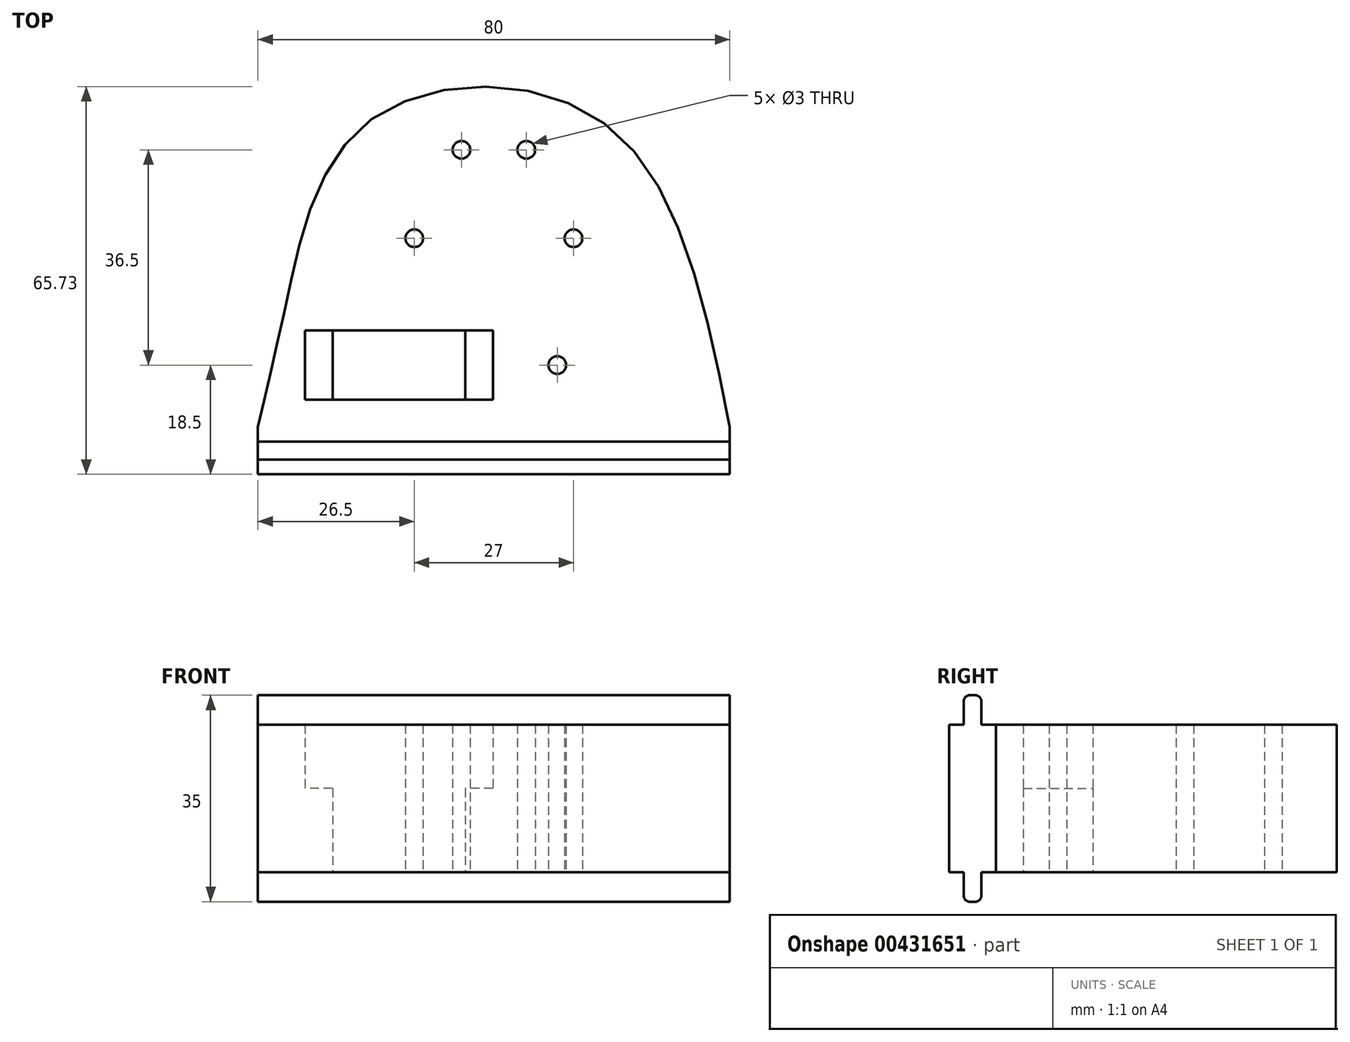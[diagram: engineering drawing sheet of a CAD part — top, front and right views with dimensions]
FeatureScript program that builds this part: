
annotation { "Feature Type Name" : "Feature", "Feature Type Description" : "" }
export const myFeature = defineFeature(function(context is Context, id is Id, definition is map)
    precondition{}
    {
        {
            var Q0;
            Q0=qCreatedBy(makeId("Top.planeOp"),FACE);
            var sketch = newSketch(context, id + "F0", { "sketchPlane" : qUnion([Q0])});
            skLineSegment(sketch, "E0.bottom", {"start": v(0, 0) * mm, "end": v(80, 0) * mm});
            skLineSegment(sketch, "E0.top", {"start": v(0, 40) * mm, "end": v(80, 40) * mm});
            skLineSegment(sketch, "E0.left", {"start": v(0, 0) * mm, "end": v(0, 40) * mm});
            skLineSegment(sketch, "E0.right", {"start": v(80, 0) * mm, "end": v(80, 40) * mm});
            skLineSegment(sketch, "E1", {"start": v(40, 0) * mm, "end": v(40, 10) * mm});
            skLineSegment(sketch, "E2", {"start": v(40, 10) * mm, "end": v(26.5, 10) * mm});
            skLineSegment(sketch, "E3", {"start": v(26.5, 10) * mm, "end": v(53.5, 10) * mm});
            skCircle(sketch, "E4", {"center": v(26.5, 10) * mm, "radius": 1.5 * mm});
            skCircle(sketch, "E5", {"center": v(53.5, 10) * mm, "radius": 1.5 * mm});
            skLineSegment(sketch, "E6.bottom", {"start": v(26.5, 10) * mm, "end": v(34.5, 10) * mm});
            skLineSegment(sketch, "E6.top", {"start": v(26.5, 25) * mm, "end": v(34.5, 25) * mm, "construction": true});
            skLineSegment(sketch, "E6.left", {"start": v(26.5, 10) * mm, "end": v(26.5, 25) * mm, "construction": true});
            skLineSegment(sketch, "E6.right", {"start": v(34.5, 10) * mm, "end": v(34.5, 25) * mm});
            skLineSegment(sketch, "E7.bottom", {"start": v(53.5, 10) * mm, "end": v(45.5, 10) * mm});
            skLineSegment(sketch, "E7.top", {"start": v(53.5, 25) * mm, "end": v(45.5, 25) * mm});
            skLineSegment(sketch, "E7.left", {"start": v(53.5, 10) * mm, "end": v(53.5, 25) * mm, "construction": true});
            skLineSegment(sketch, "E7.right", {"start": v(45.5, 10) * mm, "end": v(45.5, 25) * mm});
            skCircle(sketch, "E8", {"center": v(34.5, 25) * mm, "radius": 1.5 * mm});
            skCircle(sketch, "E9", {"center": v(45.5, 25) * mm, "radius": 1.5 * mm});
            skLineSegment(sketch, "E10.top", {"start": v(0, -30) * mm, "end": v(80, -30) * mm});
            skLineSegment(sketch, "E10.left", {"start": v(0, 0) * mm, "end": v(0, -30) * mm});
            skLineSegment(sketch, "E10.right", {"start": v(80, 0) * mm, "end": v(80, -30) * mm});
            skLineSegment(sketch, "E11.bottom", {"start": v(26.5, 10) * mm, "end": v(29.25, 10) * mm, "construction": true});
            skLineSegment(sketch, "E11.top", {"start": v(26.5, -11.5) * mm, "end": v(29.25, -11.5) * mm, "construction": true});
            skLineSegment(sketch, "E11.left", {"start": v(26.5, 10) * mm, "end": v(26.5, -11.5) * mm, "construction": true});
            skLineSegment(sketch, "E11.right", {"start": v(29.25, 10) * mm, "end": v(29.25, -11.5) * mm, "construction": true});
            skLineSegment(sketch, "E12.bottom", {"start": v(53.5, 10) * mm, "end": v(50.75, 10) * mm, "construction": true});
            skLineSegment(sketch, "E12.top", {"start": v(53.5, -11.5) * mm, "end": v(50.75, -11.5) * mm, "construction": true});
            skLineSegment(sketch, "E12.left", {"start": v(53.5, 10) * mm, "end": v(53.5, -11.5) * mm, "construction": true});
            skLineSegment(sketch, "E12.right", {"start": v(50.75, 10) * mm, "end": v(50.75, -11.5) * mm, "construction": true});
            skCircle(sketch, "E13", {"center": v(29.25, -11.5) * mm, "radius": 1.5 * mm});
            skCircle(sketch, "E14", {"center": v(50.75, -11.5) * mm, "radius": 1.5 * mm});
            skLineSegment(sketch, "E15", {"start": v(29.25, -11.5) * mm, "end": v(39.85, -11.5) * mm});
            skLineSegment(sketch, "E16", {"start": v(39.85, -11.5) * mm, "end": v(39.85, -17.4) * mm});
            skLineSegment(sketch, "E17.bottom", {"start": v(39.85, -17.4) * mm, "end": v(7.95, -17.4) * mm});
            skLineSegment(sketch, "E17.top", {"start": v(39.85, -5.6) * mm, "end": v(7.95, -5.6) * mm});
            skLineSegment(sketch, "E17.left", {"start": v(39.85, -17.4) * mm, "end": v(39.85, -5.6) * mm});
            skLineSegment(sketch, "E17.right", {"start": v(7.95, -17.4) * mm, "end": v(7.95, -5.6) * mm});
            skLineSegment(sketch, "E18", {"start": v(29.25, -11.5) * mm, "end": v(35.15, -11.5) * mm});
            skLineSegment(sketch, "E19", {"start": v(35.15, -11.5) * mm, "end": v(35.15, -17.4) * mm});
            skLineSegment(sketch, "E20.bottom", {"start": v(35.15, -17.4) * mm, "end": v(12.65, -17.4) * mm});
            skLineSegment(sketch, "E20.top", {"start": v(35.15, -5.6) * mm, "end": v(12.65, -5.6) * mm});
            skLineSegment(sketch, "E20.left", {"start": v(35.15, -17.4) * mm, "end": v(35.15, -5.6) * mm});
            skLineSegment(sketch, "E20.right", {"start": v(12.65, -17.4) * mm, "end": v(12.65, -5.6) * mm});
            skSolve(sketch);
        }
        {
            var Q0;
            Q0=makeQuery(id+"F0.imprint","IMPRINT",FACE,{"disambiguationData":[TD([[makeQuery(id+"F0.imprint","IMPRINT",EDGE,{"derivedFrom":sQuery(id+"F0.wireOp",EDGE,"E0.top")}),-1.0]])]});
            extrude(context, id + "F1", {"entities" : qUnion([Q0]), "depth" : 25 * mm});
        }
        {
            var Q0;
            Q0=makeQuery(id+"F0.imprint","IMPRINT",FACE,{"disambiguationData":[TD([[makeQuery(id+"F0.imprint","IMPRINT",EDGE,{"derivedFrom":sQuery(id+"F0.wireOp",EDGE,"E10.top")}),1.0]])]});
            extrude(context, id + "F2", {"entities" : qUnion([Q0]), "operationType" : NewBodyOperationType.ADD, "depth" : 25 * mm});
        }
        {
            var Q0;
            {var subQ0=sQuery(id+"F0.wireOp",EDGE,"E17.right");Q0=makeQuery(id+"F0.imprint","IMPRINT",FACE,{"disambiguationData":[TD([[makeQuery(id+"F0.imprint","IMPRINT",EDGE,{"derivedFrom":subQ0}),-1.0]])]});}
            var Q1;
            {var subQ0=sQuery(id+"F0.wireOp",EDGE,"E15");Q1=makeQuery(id+"F0.imprint","IMPRINT",FACE,{"disambiguationData":[TD([[makeQuery(id+"F0.imprint","IMPRINT",EDGE,{"derivedFrom":subQ0}),1.0]])]});}
            var Q2;
            {var subQ0=sQuery(id+"F0.wireOp",EDGE,"E15");Q2=makeQuery(id+"F0.imprint","IMPRINT",FACE,{"disambiguationData":[TD([[makeQuery(id+"F0.imprint","IMPRINT",EDGE,{"derivedFrom":subQ0}),-1.0]])]});}
            extrude(context, id + "F3", {"entities" : qUnion([Q0, Q1, Q2]), "operationType" : NewBodyOperationType.ADD, "depth" : 14.2 * mm});
        }
        {
            var Q0;
            {var subQ0=sQuery(id+"F0.wireOp",EDGE,"E0.bottom");Q0=makeQuery(id+"F2.boolean.opBoolean","MERGE",FACE,{"derivedFrom":[makeQuery(id+"F1.opExtrude","CAP_FACE",FACE,{"disambiguationData":[OSD([sQuery(id+"F0.wireOp",EDGE,"E0.top"),sQuery(id+"F0.wireOp",EDGE,"E0.left"),sQuery(id+"F0.wireOp",EDGE,"E0.right"),sQuery(id+"F0.wireOp",EDGE,"E4"),sQuery(id+"F0.wireOp",EDGE,"E5"),sQuery(id+"F0.wireOp",EDGE,"E8"),sQuery(id+"F0.wireOp",EDGE,"E9"),subQ0])],"isStart":false}),makeQuery(id+"F2.opExtrude","CAP_FACE",FACE,{"disambiguationData":[OSD([subQ0,sQuery(id+"F0.wireOp",EDGE,"E10.top"),sQuery(id+"F0.wireOp",EDGE,"E10.left"),sQuery(id+"F0.wireOp",EDGE,"E10.right"),sQuery(id+"F0.wireOp",EDGE,"E14"),sQuery(id+"F0.wireOp",EDGE,"E17.bottom"),sQuery(id+"F0.wireOp",EDGE,"E17.top"),sQuery(id+"F0.wireOp",EDGE,"E17.left"),sQuery(id+"F0.wireOp",EDGE,"E17.right"),sQuery(id+"F0.wireOp",EDGE,"E20.bottom"),sQuery(id+"F0.wireOp",EDGE,"E20.top")])],"isStart":false})]});}
            var sketch = newSketch(context, id + "F4", { "sketchPlane" : qUnion([Q0])});
            skLineSegment(sketch, "E21.bottom", {"start": v(0, -30) * mm, "end": v(4, -30) * mm, "construction": true});
            skLineSegment(sketch, "E21.top", {"start": v(0, -22) * mm, "end": v(4, -22) * mm, "construction": true});
            skLineSegment(sketch, "E21.left", {"start": v(0, -30) * mm, "end": v(0, -22) * mm, "construction": true});
            skLineSegment(sketch, "E21.right", {"start": v(4, -30) * mm, "end": v(4, -22) * mm, "construction": true});
            skLineSegment(sketch, "E22.bottom", {"start": v(80, -30) * mm, "end": v(61, -30) * mm, "construction": true});
            skLineSegment(sketch, "E22.top", {"start": v(80, -15) * mm, "end": v(61, -15) * mm, "construction": true});
            skLineSegment(sketch, "E22.left", {"start": v(80, -30) * mm, "end": v(80, -15) * mm, "construction": true});
            skLineSegment(sketch, "E22.right", {"start": v(61, -30) * mm, "end": v(61, -15) * mm, "construction": true});
            skLineSegment(sketch, "E23.bottom", {"start": v(80, 40) * mm, "end": v(58, 40) * mm, "construction": true});
            skLineSegment(sketch, "E23.top", {"start": v(80, 30) * mm, "end": v(58, 30) * mm, "construction": true});
            skLineSegment(sketch, "E23.left", {"start": v(80, 40) * mm, "end": v(80, 30) * mm, "construction": true});
            skLineSegment(sketch, "E23.right", {"start": v(58, 40) * mm, "end": v(58, 30) * mm, "construction": true});
            skLineSegment(sketch, "E24.bottom", {"start": v(0, 40) * mm, "end": v(19, 40) * mm, "construction": true});
            skLineSegment(sketch, "E24.top", {"start": v(0, 30) * mm, "end": v(19, 30) * mm, "construction": true});
            skLineSegment(sketch, "E24.left", {"start": v(0, 40) * mm, "end": v(0, 30) * mm, "construction": true});
            skLineSegment(sketch, "E24.right", {"start": v(19, 40) * mm, "end": v(19, 30) * mm, "construction": true});
            skLineSegment(sketch, "E25", {"start": v(0, 0) * mm, "end": v(5, 0) * mm, "construction": true});
            skLineSegment(sketch, "E26", {"start": v(80, -30) * mm, "end": v(80, -22) * mm});
            skFitSpline(sketch, "E27", {"points": [v(0, -22) * mm, v(5, 0) * mm, v(19, 30) * mm, v(58, 30) * mm, v(80, -22) * mm], "startDerivative": vector(24.26, 103.47) * mm, "endDerivative": vector(40.81, -206.26) * mm});
            skLineSegment(sketch, "E28", {"start": v(0, -30) * mm, "end": v(0, -27.5) * mm});
            skLineSegment(sketch, "E29.bottom", {"start": v(0, -27.5) * mm, "end": v(80, -27.5) * mm});
            skLineSegment(sketch, "E29.top", {"start": v(0, -24.5) * mm, "end": v(80, -24.5) * mm});
            skLineSegment(sketch, "E29.left", {"start": v(0, -27.5) * mm, "end": v(0, -24.5) * mm});
            skLineSegment(sketch, "E29.right", {"start": v(80, -27.5) * mm, "end": v(80, -24.5) * mm});
            skSolve(sketch);
        }
        {
            var Q0;
            {var subQ0=sQuery(id+"F4.wireOp",EDGE,"E27");Q0=makeQuery(id+"F4.imprint","IMPRINT",FACE,{"disambiguationData":[TD([[makeQuery(id+"F4.imprint","IMPRINT",EDGE,{"derivedFrom":subQ0}),1.0]])]});}
            extrude(context, id + "F5", {"entities" : qUnion([Q0]), "operationType" : NewBodyOperationType.REMOVE, "oppositeDirection" : true, "depth" : 25 * mm});
        }
        {
            var Q0;
            Q0=makeQuery(id+"F4.imprint","IMPRINT",FACE,{"disambiguationData":[TD([[makeQuery(id+"F4.imprint","IMPRINT",EDGE,{"derivedFrom":sQuery(id+"F4.wireOp",EDGE,"E29.bottom")}),1.0]])]});
            extrude(context, id + "F6", {"entities" : qUnion([Q0]), "operationType" : NewBodyOperationType.ADD, "depth" : 5 * mm});
        }
        {
            var Q0;
            Q0=makeQuery(id+"F6.opExtrude","CAP_FACE",FACE,{"disambiguationData":[OSD([sQuery(id+"F4.wireOp",EDGE,"E29.bottom"),sQuery(id+"F4.wireOp",EDGE,"E29.top"),sQuery(id+"F4.wireOp",EDGE,"E29.left"),sQuery(id+"F4.wireOp",EDGE,"E29.right")])],"isStart":false});
            extrude(context, id + "F7", {"entities" : qUnion([Q0]), "operationType" : NewBodyOperationType.ADD, "oppositeDirection" : true, "depth" : 35 * mm});
        }
        {
            var Q0;
            Q0=makeQuery(id+"F6.opExtrude","CAP_EDGE",EDGE,{"disambiguationData":[OSD([sQuery(id+"F4.wireOp",EDGE,"E29.top")])],"isStart":false});
            var Q1;
            Q1=makeQuery(id+"F6.opExtrude","CAP_EDGE",EDGE,{"disambiguationData":[OSD([sQuery(id+"F4.wireOp",EDGE,"E29.bottom")])],"isStart":false});
            var Q2;
            Q2=makeQuery(id+"F7.opExtrude","CAP_EDGE",EDGE,{"disambiguationData":[OSD([sQuery(id+"F4.wireOp",EDGE,"E29.top")])],"isStart":false});
            var Q3;
            Q3=makeQuery(id+"F7.opExtrude","CAP_EDGE",EDGE,{"disambiguationData":[OSD([sQuery(id+"F4.wireOp",EDGE,"E29.bottom")])],"isStart":false});
            fillet(context, id + "F8", {"entities" : qUnion([Q0, Q1, Q2, Q3]), "radius" : 1 * mm, "tangentPropagation" : true, "allowEdgeOverflow" : false});
        }
    });
